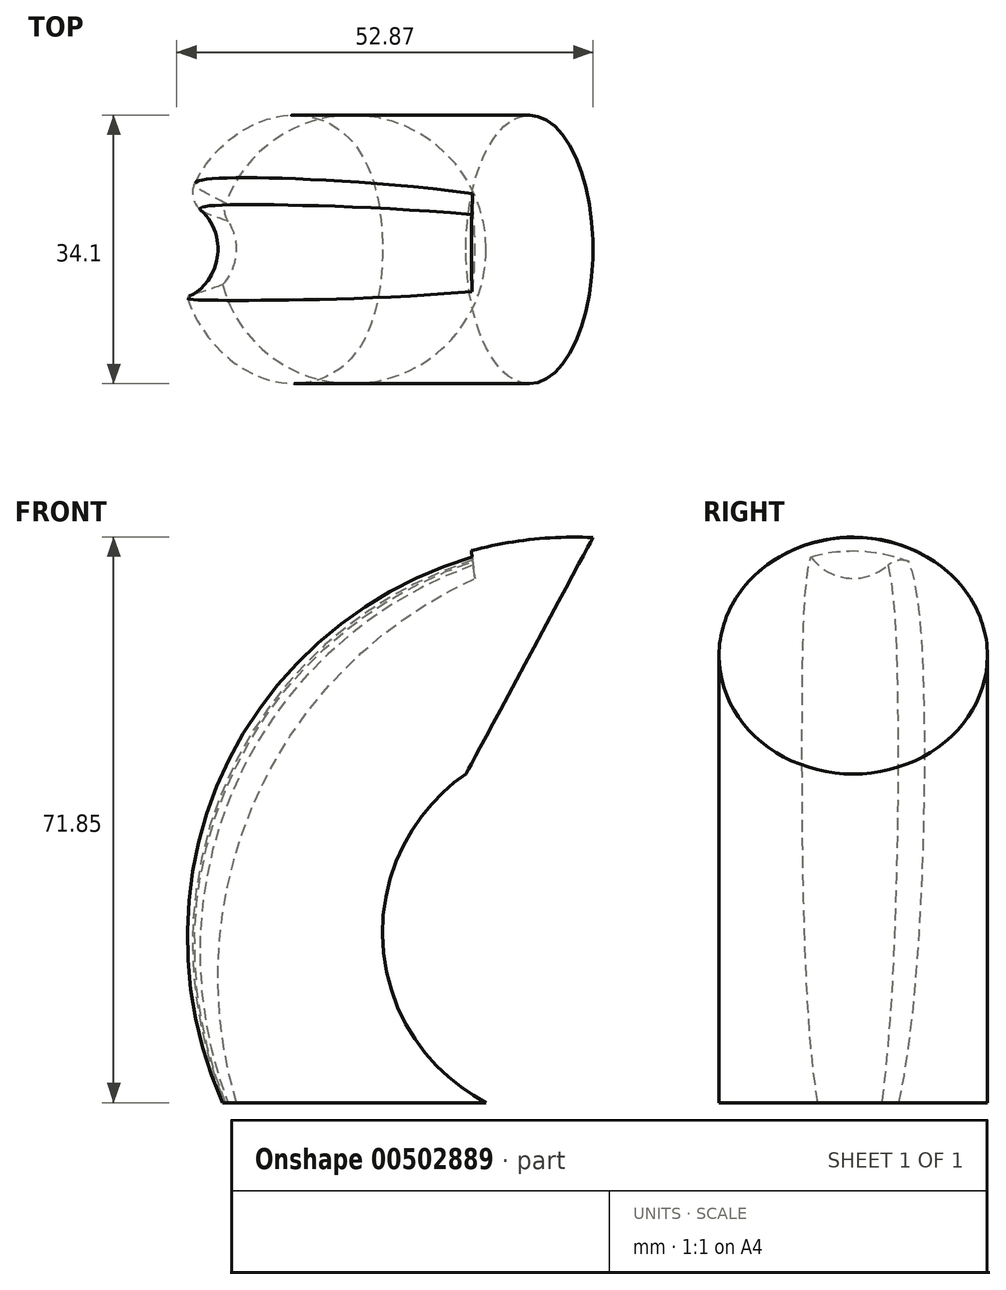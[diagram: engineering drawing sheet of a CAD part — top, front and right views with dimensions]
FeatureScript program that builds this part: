
annotation { "Feature Type Name" : "Feature", "Feature Type Description" : "" }
export const myFeature = defineFeature(function(context is Context, id is Id, definition is map)
    precondition{}
    {
        {
            var Q0;
            Q0=qCreatedBy(makeId("Top.planeOp"),FACE);
            var sketch = newSketch(context, id + "F0", { "sketchPlane" : qUnion([Q0])});
            skCircle(sketch, "E0", {"center": v(0, 0) * mm, "radius": 17.05 * mm});
            skSolve(sketch);
        }
        {
            var Q0;
            Q0=qCreatedBy(makeId("Front.planeOp"),FACE);
            var sketch = newSketch(context, id + "F1", { "sketchPlane" : qUnion([Q0])});
            skArc(sketch, "E1", {"start": v(22.55, 56.78) * mm, "mid": v(-4.83, 34.78) * mm, "end": v(0, 0) * mm});
            skSolve(sketch);
        }
        {
            var Q0;
            Q0=makeQuery(id+"F0.imprint","IMPRINT",FACE,{"disambiguationData":[TD([[makeQuery(id+"F0.imprint","IMPRINT",EDGE,{"derivedFrom":sQuery(id+"F0.wireOp",EDGE,"E0")}),1.0]])]});
            var Q1;
            Q1=sQuery(id+"F1.wireOp",EDGE,"E1");
            sweep(context, id + "F2", {"profiles" : qUnion([Q0]), "path" : qUnion([Q1])});
        }
        {
            var Q0;
            Q0=qCreatedBy(makeId("Top.planeOp"),FACE);
            var sketch = newSketch(context, id + "F3", { "sketchPlane" : qUnion([Q0])});
            skCircle(sketch, "E2", {"center": v(-21.24, 0) * mm, "radius": 6.58 * mm});
            skSolve(sketch);
        }
        {
            var Q0;
            Q0=qCreatedBy(makeId("Front.planeOp"),FACE);
            var sketch = newSketch(context, id + "F4", { "sketchPlane" : qUnion([Q0])});
            skArc(sketch, "E3", {"start": v(14.75, 73.12) * mm, "mid": v(-16.98, 43.33) * mm, "end": v(-21.24, 0) * mm});
            skSolve(sketch);
        }
        {
            var Q0;
            Q0=makeQuery(id+"F3.imprint","IMPRINT",FACE,{"disambiguationData":[TD([[makeQuery(id+"F3.imprint","IMPRINT",EDGE,{"derivedFrom":sQuery(id+"F3.wireOp",EDGE,"E2")}),1.0]])]});
            var Q1;
            Q1=sQuery(id+"F4.wireOp",EDGE,"E3");
            sweep(context, id + "F5", {"operationType" : NewBodyOperationType.REMOVE, "profiles" : qUnion([Q0]), "path" : qUnion([Q1])});
        }
        {
            var Q0;
            Q0=makeQuery(id+"F5.boolean.opBoolean","INTERSECT",EDGE,{"disambiguationData":[OD(1.0)],"derivedFrom":[makeQuery(id+"F2.opSweep","SWEPT_FACE",FACE,{"disambiguationData":[OSD([sQuery(id+"F0.wireOp",EDGE,"E0"),sQuery(id+"F1.wireOp",EDGE,"E1")])]}),makeQuery(id+"F5.opSweep","SWEPT_FACE",FACE,{"disambiguationData":[OSD([sQuery(id+"F3.wireOp",EDGE,"E2"),sQuery(id+"F4.wireOp",EDGE,"E3")])]})]});
            fillet(context, id + "F6", {"entities" : qUnion([Q0]), "radius" : 2.54 * mm, "tangentPropagation" : true, "allowEdgeOverflow" : false});
        }
    });
